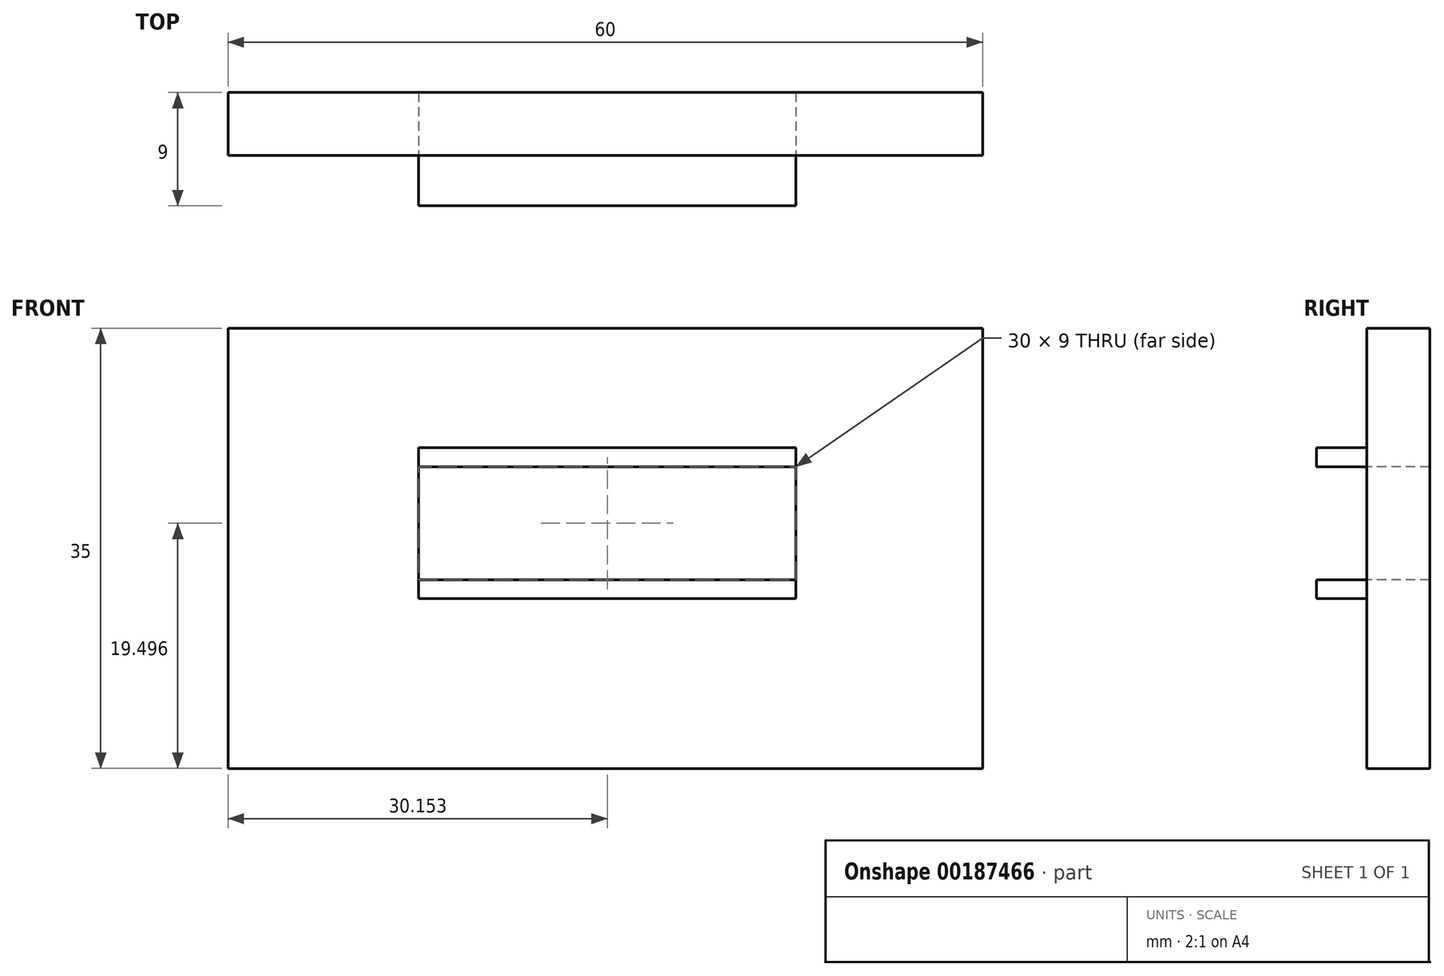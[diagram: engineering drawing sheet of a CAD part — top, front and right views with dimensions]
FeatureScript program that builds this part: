
annotation { "Feature Type Name" : "Feature", "Feature Type Description" : "" }
export const myFeature = defineFeature(function(context is Context, id is Id, definition is map)
    precondition{}
    {
        {
            var Q0;
            Q0=qCreatedBy(makeId("Front.planeOp"),FACE);
            var sketch = newSketch(context, id + "F0", { "sketchPlane" : qUnion([Q0])});
            skLineSegment(sketch, "E0", {"start": v(-15.14, 6) * mm, "end": v(-15.14, -6) * mm});
            skLineSegment(sketch, "E1", {"start": v(14.86, -6) * mm, "end": v(14.86, 6) * mm});
            skLineSegment(sketch, "E2", {"start": v(-15.14, 6) * mm, "end": v(14.86, 6) * mm});
            skLineSegment(sketch, "E3", {"start": v(14.86, -6) * mm, "end": v(-15.14, -6) * mm});
            skLineSegment(sketch, "E4", {"start": v(-15.14, 6) * mm, "end": v(-15.14, 4.5) * mm});
            skLineSegment(sketch, "E5", {"start": v(-15.14, 4.5) * mm, "end": v(14.86, 4.5) * mm});
            skLineSegment(sketch, "E6", {"start": v(14.86, 4.5) * mm, "end": v(14.86, 6) * mm});
            skLineSegment(sketch, "E7", {"start": v(-15.14, -6) * mm, "end": v(-15.14, -4.5) * mm});
            skLineSegment(sketch, "E8", {"start": v(-15.14, -4.5) * mm, "end": v(14.86, -4.5) * mm});
            skLineSegment(sketch, "E9", {"start": v(14.86, -4.5) * mm, "end": v(14.86, -6) * mm});
            skLineSegment(sketch, "E10", {"start": v(-30.3, -19.5) * mm, "end": v(-30.3, 15.5) * mm});
            skLineSegment(sketch, "E11", {"start": v(-30.3, 15.5) * mm, "end": v(29.7, 15.5) * mm});
            skLineSegment(sketch, "E12", {"start": v(29.7, 15.5) * mm, "end": v(29.7, -19.5) * mm});
            skLineSegment(sketch, "E13", {"start": v(-30.3, -19.5) * mm, "end": v(29.7, -19.5) * mm});
            skSolve(sketch);
        }
        {
            var Q0;
            Q0=makeQuery(id+"F0.imprint","IMPRINT",FACE,{"disambiguationData":[TD([[makeQuery(id+"F0.imprint","IMPRINT",EDGE,{"derivedFrom":sQuery(id+"F0.wireOp",EDGE,"E2")}),-1.0]])]});
            var Q1;
            Q1=makeQuery(id+"F0.imprint","IMPRINT",FACE,{"disambiguationData":[TD([[makeQuery(id+"F0.imprint","IMPRINT",EDGE,{"derivedFrom":sQuery(id+"F0.wireOp",EDGE,"E3")}),-1.0]])]});
            extrude(context, id + "F1", {"entities" : qUnion([Q0, Q1]), "depth" : 4 * mm});
        }
        {
            var Q0;
            Q0 = qSketchRegion(id + "F0", true);
            var Q1;
            Q1=makeQuery(id+"F0.imprint","IMPRINT",FACE,{"disambiguationData":[TD([[makeQuery(id+"F0.imprint","IMPRINT",EDGE,{"derivedFrom":sQuery(id+"F0.wireOp",EDGE,"E2")}),-1.0]])]});
            var Q2;
            Q2=makeQuery(id+"F0.imprint","IMPRINT",FACE,{"disambiguationData":[TD([[makeQuery(id+"F0.imprint","IMPRINT",EDGE,{"derivedFrom":sQuery(id+"F0.wireOp",EDGE,"E3")}),-1.0]])]});
            extrude(context, id + "F2", {"entities" : qUnion([Q0, Q1, Q2]), "oppositeDirection" : true, "depth" : 5 * mm});
        }
    });
